# Revit family: Artek_Lighting_Pendant Light A330S “Golden Bell“_A330S “Golden Bell“_quick_ship
name_source: partatom
category: Lighting Fixtures
revit_build: Autodesk Revit 2018 (Build: 20170223_1515(x64)
units: mm (PartAtom-declared; Revit-internal decimal feet)

## family parameters
Always vertical = Yes
Cut with Voids When Loaded = No
Light Source = Yes
OmniClass Number = 23.80.70.00
OmniClass Title = Lighting
Part Type = Normal
Room Calculation Point = No
Round Connector Dimension = Use Diameter
Shared = No
Work Plane-Based = No

## types (5) — shared parameters
AssetType = Fixed
BIMObjectName = Artek_Lighting_Pendant Light A330S “Golden Bell“_A330S “Golden Bell“_quick_ship
Brand = Artek
Category = Lighting
Collection = Pendant Lights
Color Filter = 16777215
ConvergoRefNr = 0190-2009-0054-FI
Description = Nicknamed “Golden Bell,” Pendant Light A330S has a sculptural quality that can be appreciated whether the light is switched on or off.
Designer = Alvar Aalto
Dimming Lamp Color Temperature Shift = <None>
DurationUnit = Years
HasProtectiveEarth = No
IP_Code = IP20
IfcExportAs = IfcLightFixtureType
IfcExportType = NOTDEFINED
InsulationStandardClass = Class II
Light Source Symbol Size = 610 mm
LightFixtureMountingType = Suspended
LightFixturePlacingType = Ceiling
Manufacturer = Artek
ManufacturerName = Artek
ManufacturerURL = https://www.artek.fi
ManufacturersSpecificInformation = This luminaire is compatible with bulbs of the energy classes: A to G
NBSDescription = General purpose luminaires
NBSReference = 90-60-50/405
Name = A330S "Golden Bell"
NominalCurrent = 0 A
NominalDiameter = 164 mm  [stored 0.538058 ft]
NominalFrequencyRange = 60 Hz
NominalLength = 164 mm  [stored 0.538058 ft]
NominalRadius = 82 mm  [stored 0.269029 ft]
NominalVoltage = 240 V
NominalVoltageCalc = 0 V
NominalWidth = 164 mm  [stored 0.538058 ft]
NumberOfPoles = 1
PhaseAngle = 0.00°
ProductInformation = Nicknamed “Golden Bell,” Pendant Light A330S has a sculptural quality that can be appreciated whether the light is switched on or off.
Shape = Sculptured
Size = 170x200x170 mm
Socket = E27
TotalWattage = 12 W
URL = https://www.artek.fi
Uniclass2 = Pr_70_70_49_86
Uniclass2015Description = Pendant  luminaires
Uniclass2015Reference = Pr_70_70_48_62
UsageCurrent = 0 A
Version = 1
VersionDate = 11/3/2020
WarrantyDurationUnit = Years
zero-valued in all types: DefaultElevation, ElectricalDeviceNominalPower, MaintenanceFactor, NumberOfSources

## per-type parameters (varying)
| type | ArticleNumber | Color | LightFixtureMainMaterial | LightFixtureSecondaryMaterial | LightFixtureTertiaryMaterial | Material | ModelNumber |
| A330S "Golden Bell", 29100380 | 29100380 | Brass | Brass | Black plastic | Brass | Brass | 29100380 |
| A330S "Golden Bell", 29100301 | 29100301 | Brass | Brass | White plastic | White Steel | Brass | 29100301 |
| A330S "Golden Bell", 29100302 | 29100302 | Chrome | Chrome | White plastic | White Steel | Steel, powder coated | 29100302 |
| A330S "Golden Bell", 29100303 | 29100303 | Black | Black laquered | Black plastic | White Steel | Steel, powder coated | 29100303 |
| A330S "Golden Bell", 29100304 | 29100304 | White | White Steel | White plastic | White Steel | Steel, powder coated | 29100304 |

note: column(s) folded — value = type name in every type: Model

note: [stored X ft] marks values corroborated as IEEE doubles in the binary element streams (Revit-internal decimal feet)

## geometry (parser evidence)
native form markers: Sweep x6
no freeform markers — native parametric forms only
